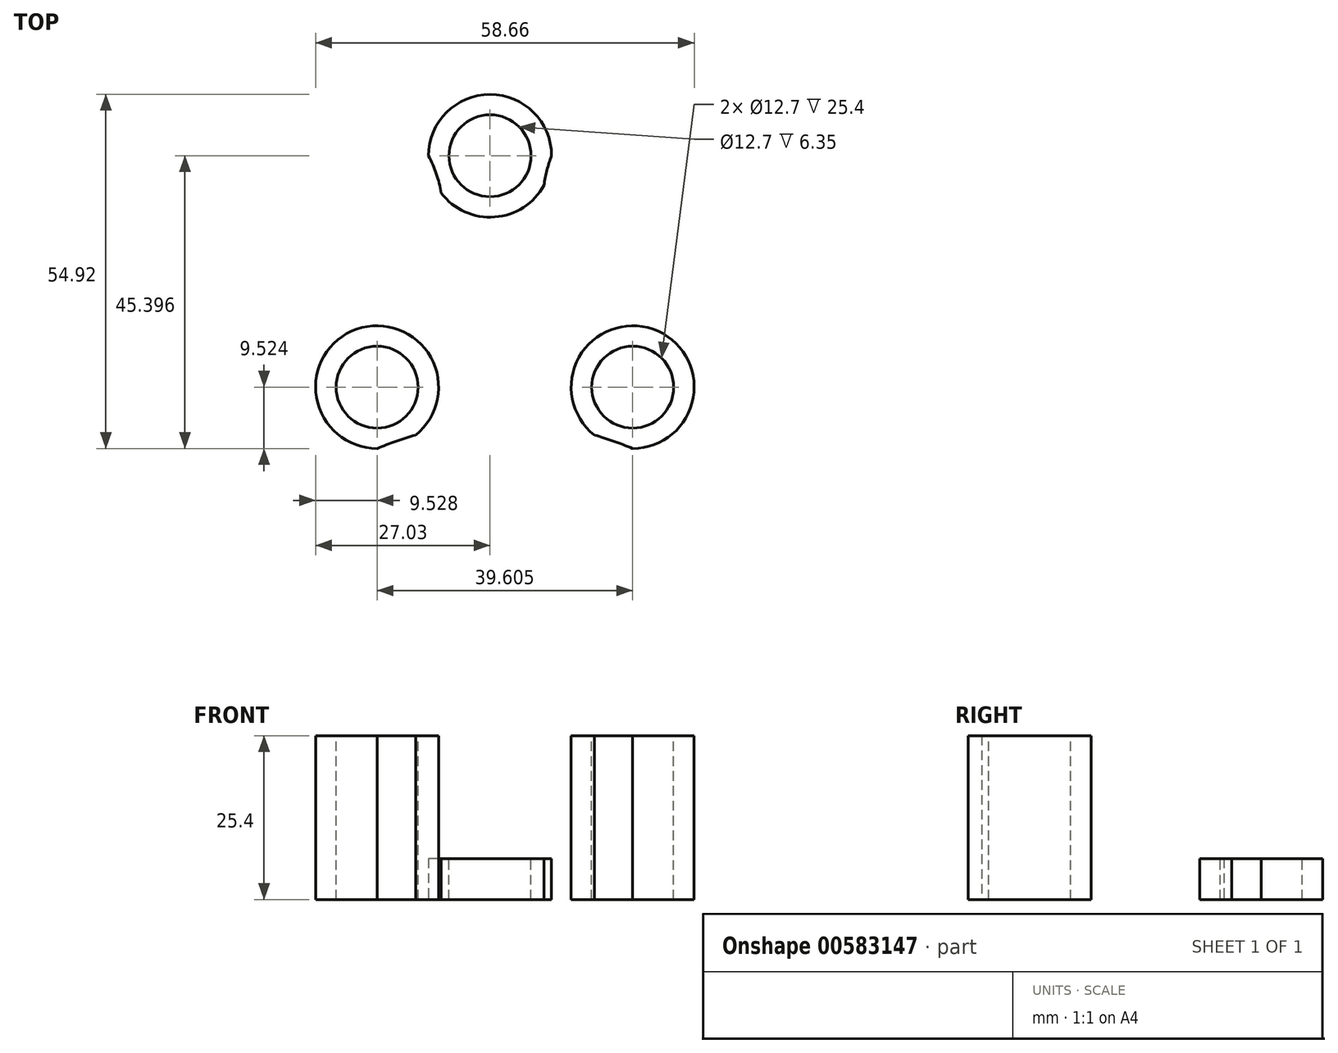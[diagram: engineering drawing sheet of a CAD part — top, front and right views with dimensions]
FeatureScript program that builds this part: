
annotation { "Feature Type Name" : "Feature", "Feature Type Description" : "" }
export const myFeature = defineFeature(function(context is Context, id is Id, definition is map)
    precondition{}
    {
        {
            var Q0;
            Q0=qCreatedBy(makeId("Top.planeOp"),FACE);
            var sketch = newSketch(context, id + "F0", { "sketchPlane" : qUnion([Q0])});
            skCircle(sketch, "E0", {"center": v(-34.1, 34.18) * mm, "radius": 9.53 * mm});
            skArc(sketch, "E1", {"start": v(-24.57, 34.18) * mm, "mid": v(-23.95, 18.3) * mm, "end": v(-12, 7.83) * mm});
            skCircle(sketch, "E2", {"center": v(-12, -1.7) * mm, "radius": 9.53 * mm});
            skCircle(sketch, "E3", {"center": v(-51.6, -1.7) * mm, "radius": 9.53 * mm});
            skArc(sketch, "E4", {"start": v(-51.6, 7.83) * mm, "mid": v(-42.23, 19.37) * mm, "end": v(-43.62, 34.18) * mm});
            skArc(sketch, "E5", {"start": v(-12, -11.22) * mm, "mid": v(-31.8, -7.2) * mm, "end": v(-51.6, -11.22) * mm});
            skSolve(sketch);
        }
        {
            var Q0;
            {var subQ0=sQuery(id+"F0.wireOp",EDGE,"E4");var subQ9=sQuery(id+"F0.wireOp",EDGE,"E0");var subQ11=makeQuery(id+"F0.imprint","INTERSECT",VERTEX,{"disambiguationData":[OD(1.0)],"derivedFrom":[subQ9,subQ0]});Q0=makeQuery(id+"F0.imprint","IMPRINT",FACE,{"disambiguationData":[TD([[makeQuery(id+"F0.imprint","IMPRINT",EDGE,{"disambiguationData":[TD([[subQ11,-1.0]])],"derivedFrom":subQ9}),-1.0]])]});}
            var Q1;
            {var subQ0=sQuery(id+"F0.wireOp",EDGE,"E3");var subQ1=makeQuery(id+"F0.imprint","INTERSECT",VERTEX,{"derivedFrom":[subQ0,sQuery(id+"F0.wireOp",EDGE,"E4")]});Q1=makeQuery(id+"F0.imprint","IMPRINT",FACE,{"disambiguationData":[TD([[makeQuery(id+"F0.imprint","IMPRINT",EDGE,{"disambiguationData":[TD([[subQ1,-1.0]])],"derivedFrom":subQ0}),1.0]])]});}
            var Q2;
            {var subQ0=sQuery(id+"F0.wireOp",EDGE,"E2");var subQ1=makeQuery(id+"F0.imprint","INTERSECT",VERTEX,{"derivedFrom":[sQuery(id+"F0.wireOp",EDGE,"E1"),subQ0]});Q2=makeQuery(id+"F0.imprint","IMPRINT",FACE,{"disambiguationData":[TD([[makeQuery(id+"F0.imprint","IMPRINT",EDGE,{"disambiguationData":[TD([[subQ1,-1.0]])],"derivedFrom":subQ0}),1.0]])]});}
            var Q3;
            {var subQ0=sQuery(id+"F0.wireOp",EDGE,"E1");var subQ1=sQuery(id+"F0.wireOp",EDGE,"E0");var subQ2=makeQuery(id+"F0.imprint","INTERSECT",VERTEX,{"disambiguationData":[OD(0.0)],"derivedFrom":[subQ1,subQ0]});Q3=makeQuery(id+"F0.imprint","IMPRINT",FACE,{"disambiguationData":[TD([[makeQuery(id+"F0.imprint","IMPRINT",EDGE,{"disambiguationData":[TD([[subQ2,-1.0]])],"derivedFrom":subQ1}),1.0]])]});}
            extrude(context, id + "F1", {"entities" : qUnion([Q0, Q1, Q2, Q3]), "depth" : 25.4 * mm, "offsetDistance" : 25.4 * mm});
        }
        {
            var Q0;
            Q0=makeQuery(id+"F1.opExtrude","CAP_FACE",FACE,{"disambiguationData":[OSD([sQuery(id+"F0.wireOp",EDGE,"E0"),sQuery(id+"F0.wireOp",EDGE,"E1"),sQuery(id+"F0.wireOp",EDGE,"E2"),sQuery(id+"F0.wireOp",EDGE,"E3"),sQuery(id+"F0.wireOp",EDGE,"E4"),sQuery(id+"F0.wireOp",EDGE,"E5")])],"isStart":false});
            var sketch = newSketch(context, id + "F2", { "sketchPlane" : qUnion([Q0])});
            skCircle(sketch, "E6", {"center": v(-51.6, -1.7) * mm, "radius": 6.35 * mm});
            skCircle(sketch, "E7", {"center": v(-12, -1.7) * mm, "radius": 6.35 * mm});
            skCircle(sketch, "E8", {"center": v(-34.1, 34.18) * mm, "radius": 6.35 * mm});
            skSolve(sketch);
        }
        {
            var Q0;
            Q0=makeQuery(id+"F2.imprint","IMPRINT",FACE,{"disambiguationData":[TD([[makeQuery(id+"F2.imprint","IMPRINT",EDGE,{"derivedFrom":sQuery(id+"F2.wireOp",EDGE,"E6")}),1.0]])]});
            var Q1;
            Q1=makeQuery(id+"F2.imprint","IMPRINT",FACE,{"disambiguationData":[TD([[makeQuery(id+"F2.imprint","IMPRINT",EDGE,{"derivedFrom":sQuery(id+"F2.wireOp",EDGE,"E7")}),1.0]])]});
            var Q2;
            Q2=makeQuery(id+"F2.imprint","IMPRINT",FACE,{"disambiguationData":[TD([[makeQuery(id+"F2.imprint","IMPRINT",EDGE,{"derivedFrom":sQuery(id+"F2.wireOp",EDGE,"E8")}),1.0]])]});
            extrude(context, id + "F3", {"entities" : qUnion([Q0, Q1, Q2]), "operationType" : NewBodyOperationType.REMOVE, "endBound" : BoundingType.THROUGH_ALL, "oppositeDirection" : true, "depth" : 25.4 * mm, "offsetDistance" : 25.4 * mm});
        }
        {
            var Q0;
            Q0=makeQuery(id+"F1.opExtrude","CAP_FACE",FACE,{"disambiguationData":[OSD([sQuery(id+"F0.wireOp",EDGE,"E0"),sQuery(id+"F0.wireOp",EDGE,"E1"),sQuery(id+"F0.wireOp",EDGE,"E2"),sQuery(id+"F0.wireOp",EDGE,"E3"),sQuery(id+"F0.wireOp",EDGE,"E4"),sQuery(id+"F0.wireOp",EDGE,"E5")])],"isStart":false});
            extrude(context, id + "F4", {"entities" : qUnion([Q0]), "operationType" : NewBodyOperationType.REMOVE, "oppositeDirection" : true, "depth" : 19.05 * mm, "offsetDistance" : 25.4 * mm});
        }
        {
            var Q0;
            Q0=makeQuery(id+"F4.boolean.opBoolean","COPY",FACE,{"derivedFrom":makeQuery(id+"F4.opExtrude","CAP_FACE",FACE,{"disambiguationData":[OSD([sQuery(id+"F0.wireOp",EDGE,"E0"),sQuery(id+"F0.wireOp",EDGE,"E1"),sQuery(id+"F0.wireOp",EDGE,"E2"),sQuery(id+"F0.wireOp",EDGE,"E3"),sQuery(id+"F0.wireOp",EDGE,"E4"),sQuery(id+"F0.wireOp",EDGE,"E5")])],"isStart":false})});
            var sketch = newSketch(context, id + "F5", { "sketchPlane" : qUnion([Q0])});
            skCircle(sketch, "E9", {"center": v(-31.78, 13.12) * mm, "radius": 6.35 * mm});
            skSolve(sketch);
        }
        {
            var Q0;
            Q0=makeQuery(id+"F5.imprint","IMPRINT",FACE,{"disambiguationData":[TD([[makeQuery(id+"F5.imprint","IMPRINT",EDGE,{"derivedFrom":sQuery(id+"F5.wireOp",EDGE,"E9")}),1.0]])]});
            extrude(context, id + "F6", {"entities" : qUnion([Q0]), "operationType" : NewBodyOperationType.REMOVE, "endBound" : BoundingType.THROUGH_ALL, "oppositeDirection" : true, "depth" : 25.4 * mm, "offsetDistance" : 25.4 * mm});
        }
    });
